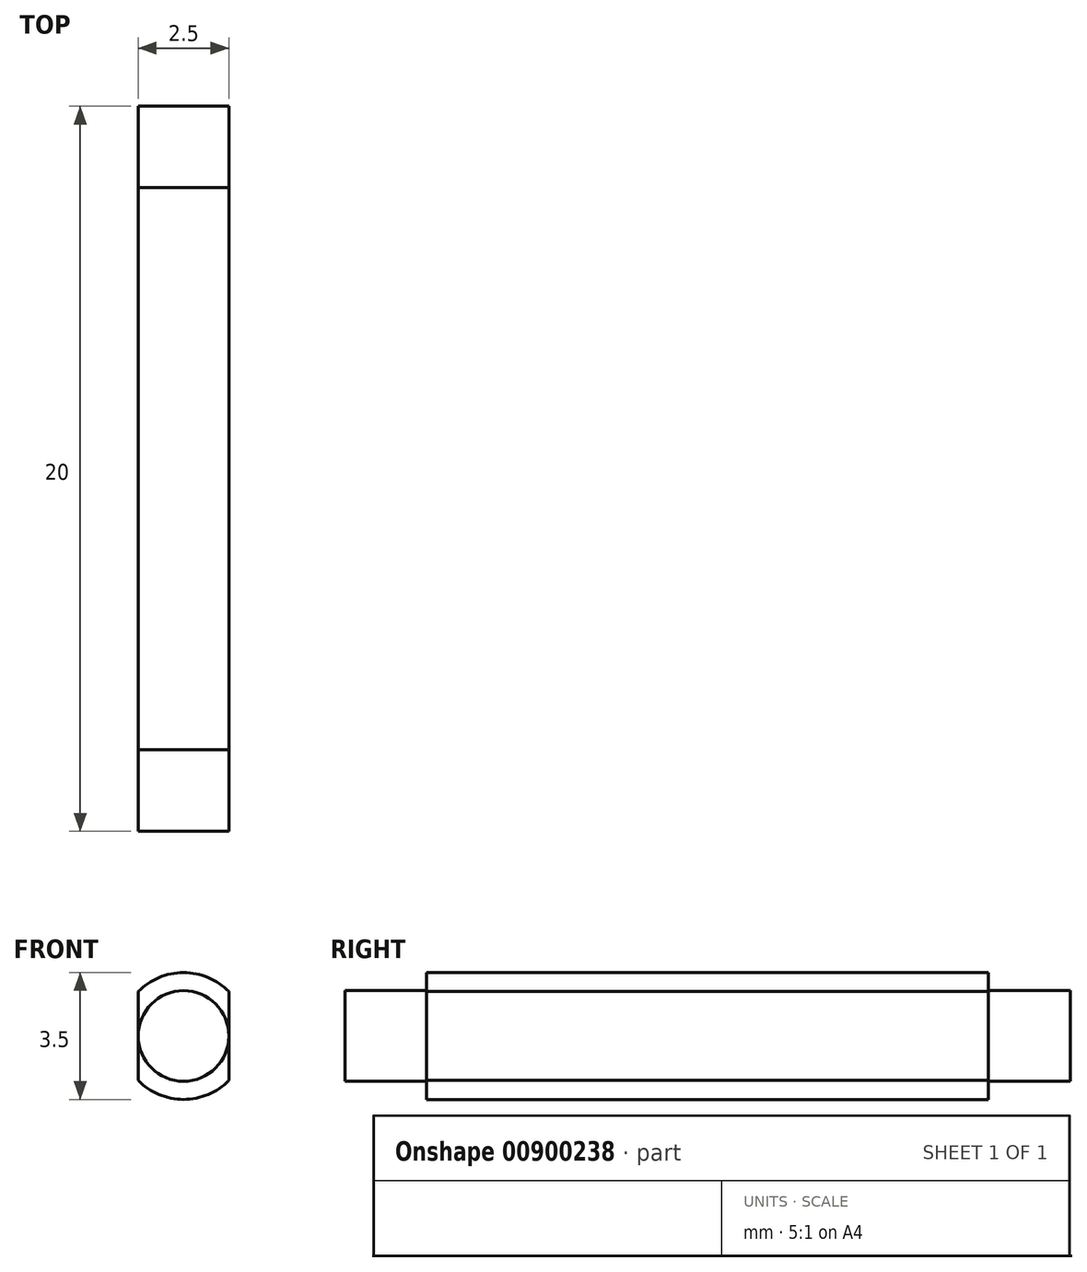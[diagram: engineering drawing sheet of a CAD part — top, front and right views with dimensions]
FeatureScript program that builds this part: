
annotation { "Feature Type Name" : "Feature", "Feature Type Description" : "" }
export const myFeature = defineFeature(function(context is Context, id is Id, definition is map)
    precondition{}
    {
        {
            var Q0;
            Q0=qCreatedBy(makeId("Front.planeOp"),FACE);
            var sketch = newSketch(context, id + "F0", { "sketchPlane" : qUnion([Q0])});
            skArc(sketch, "E0", {"start": v(-1.25, -1.22) * mm, "mid": v(0, -1.75) * mm, "end": v(1.25, -1.22) * mm});
            skLineSegment(sketch, "E1", {"start": v(-1.25, 1.22) * mm, "end": v(-1.25, -1.22) * mm});
            skLineSegment(sketch, "E2", {"start": v(1.25, 1.22) * mm, "end": v(1.25, -1.22) * mm});
            skArc(sketch, "E3.trimOffspring", {"start": v(1.25, 1.22) * mm, "mid": v(0, 1.75) * mm, "end": v(-1.25, 1.22) * mm});
            skSolve(sketch);
        }
        {
            var Q0;
            Q0 = qSketchRegion(id + "F0", true);
            extrude(context, id + "F1", {"entities" : qUnion([Q0]), "depth" : 15.5 * mm, "offsetDistance" : 25 * mm, "symmetric" : true});
        }
        {
            var Q0;
            Q0=qCreatedBy(makeId("Front.planeOp"),FACE);
            var sketch = newSketch(context, id + "F2", { "sketchPlane" : qUnion([Q0])});
            skCircle(sketch, "E4", {"center": v(0, 0) * mm, "radius": 1.25 * mm});
            skSolve(sketch);
        }
        {
            var Q0;
            Q0 = qSketchRegion(id + "F2", true);
            extrude(context, id + "F3", {"entities" : qUnion([Q0]), "operationType" : NewBodyOperationType.ADD, "depth" : 20 * mm, "offsetDistance" : 25 * mm, "symmetric" : true});
        }
    });
